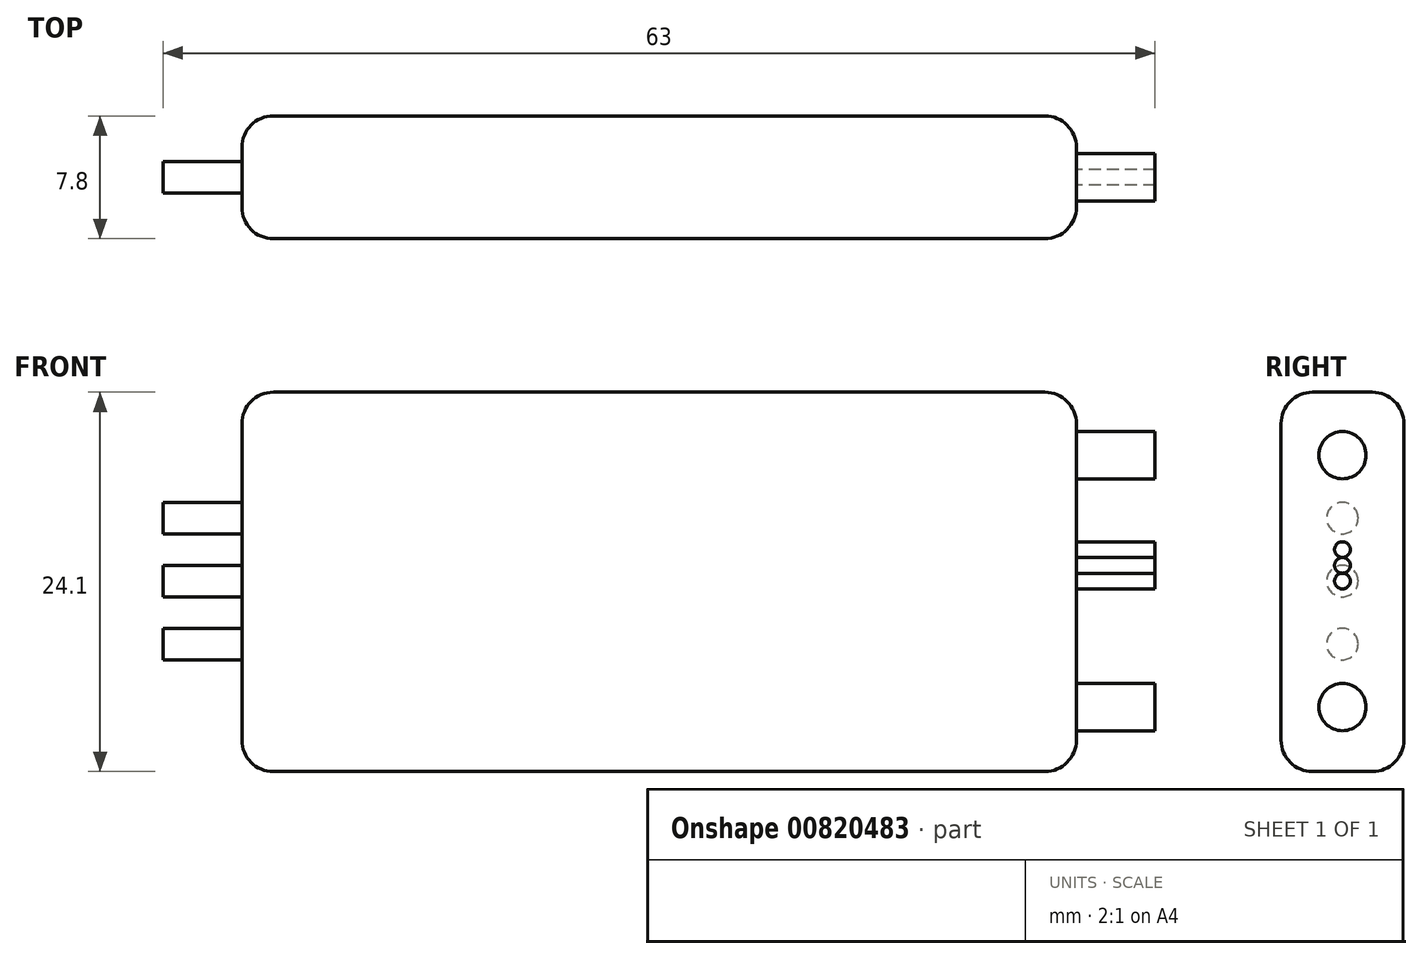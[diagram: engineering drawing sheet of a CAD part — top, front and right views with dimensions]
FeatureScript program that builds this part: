
annotation { "Feature Type Name" : "Feature", "Feature Type Description" : "" }
export const myFeature = defineFeature(function(context is Context, id is Id, definition is map)
    precondition{}
    {
        {
            var Q0;
            Q0=qCreatedBy(makeId("Front.planeOp"),FACE);
            var sketch = newSketch(context, id + "F0", { "sketchPlane" : qUnion([Q0])});
            skLineSegment(sketch, "E0.bottom", {"start": v(0, 0) * mm, "end": v(53, 0) * mm});
            skLineSegment(sketch, "E0.top", {"start": v(0, 24.1) * mm, "end": v(53, 24.1) * mm});
            skLineSegment(sketch, "E0.left", {"start": v(0, 0) * mm, "end": v(0, 24.1) * mm});
            skLineSegment(sketch, "E0.right", {"start": v(53, 0) * mm, "end": v(53, 24.1) * mm});
            skSolve(sketch);
        }
        {
            var Q0;
            Q0=makeQuery(id+"F0.imprint","IMPRINT",FACE,{"disambiguationData":[TD([[makeQuery(id+"F0.imprint","IMPRINT",EDGE,{"derivedFrom":sQuery(id+"F0.wireOp",EDGE,"E0.bottom")}),1.0]])]});
            extrude(context, id + "F1", {"entities" : qUnion([Q0]), "depth" : 7.8 * mm, "offsetDistance" : 25 * mm});
        }
        {
            var Q0;
            Q0=makeQuery(id+"F1.opExtrude","SWEPT_EDGE",EDGE,{"disambiguationData":[OSD([sQuery(id+"F0.wireOp",EDGE,"E0.bottom"),sQuery(id+"F0.wireOp",EDGE,"E0.right")])]});
            var Q1;
            Q1=makeQuery(id+"F1.opExtrude","SWEPT_EDGE",EDGE,{"disambiguationData":[OSD([sQuery(id+"F0.wireOp",EDGE,"E0.top"),sQuery(id+"F0.wireOp",EDGE,"E0.left")])]});
            var Q2;
            Q2=makeQuery(id+"F1.opExtrude","SWEPT_EDGE",EDGE,{"disambiguationData":[OSD([sQuery(id+"F0.wireOp",EDGE,"E0.top"),sQuery(id+"F0.wireOp",EDGE,"E0.right")])]});
            var Q3;
            Q3=makeQuery(id+"F1.opExtrude","SWEPT_EDGE",EDGE,{"disambiguationData":[OSD([sQuery(id+"F0.wireOp",EDGE,"E0.bottom"),sQuery(id+"F0.wireOp",EDGE,"E0.left")])]});
            var Q4;
            Q4=makeQuery(id+"F1.opExtrude","CAP_EDGE",EDGE,{"disambiguationData":[OSD([sQuery(id+"F0.wireOp",EDGE,"E0.bottom")])],"isStart":true});
            var Q5;
            Q5=makeQuery(id+"F1.opExtrude","CAP_EDGE",EDGE,{"disambiguationData":[OSD([sQuery(id+"F0.wireOp",EDGE,"E0.bottom")])],"isStart":false});
            var Q6;
            Q6=makeQuery(id+"F1.opExtrude","CAP_EDGE",EDGE,{"disambiguationData":[OSD([sQuery(id+"F0.wireOp",EDGE,"E0.top")])],"isStart":true});
            var Q7;
            Q7=makeQuery(id+"F1.opExtrude","CAP_EDGE",EDGE,{"disambiguationData":[OSD([sQuery(id+"F0.wireOp",EDGE,"E0.top")])],"isStart":false});
            var Q8;
            Q8=makeQuery(id+"F1.opExtrude","CAP_EDGE",EDGE,{"disambiguationData":[OSD([sQuery(id+"F0.wireOp",EDGE,"E0.left")])],"isStart":true});
            var Q9;
            Q9=makeQuery(id+"F1.opExtrude","CAP_EDGE",EDGE,{"disambiguationData":[OSD([sQuery(id+"F0.wireOp",EDGE,"E0.left")])],"isStart":false});
            var Q10;
            Q10=makeQuery(id+"F1.opExtrude","CAP_EDGE",EDGE,{"disambiguationData":[OSD([sQuery(id+"F0.wireOp",EDGE,"E0.right")])],"isStart":true});
            var Q11;
            Q11=makeQuery(id+"F1.opExtrude","CAP_EDGE",EDGE,{"disambiguationData":[OSD([sQuery(id+"F0.wireOp",EDGE,"E0.right")])],"isStart":false});
            fillet(context, id + "F2", {"entities" : qUnion([Q0, Q1, Q2, Q3, Q4, Q5, Q6, Q7, Q8, Q9, Q10, Q11]), "radius" : 2 * mm, "tangentPropagation" : true, "allowEdgeOverflow" : false});
        }
        {
            var Q0;
            Q0=makeQuery(id+"F1.opExtrude","SWEPT_FACE",FACE,{"disambiguationData":[OSD([sQuery(id+"F0.wireOp",EDGE,"E0.left")])]});
            var sketch = newSketch(context, id + "F3", { "sketchPlane" : qUnion([Q0])});
            skCircle(sketch, "E1", {"center": v(3.9, 16.1) * mm, "radius": 1 * mm});
            skCircle(sketch, "E2.0.1.0", {"center": v(3.9, 12.1) * mm, "radius": 1 * mm});
            skCircle(sketch, "E2.0.2.0", {"center": v(3.9, 8.1) * mm, "radius": 1 * mm});
            skLineSegment(sketch, "E2.direction1", {"start": v(3.9, 16.1) * mm, "end": v(6.9, 16.1) * mm, "construction": true});
            skLineSegment(sketch, "E2.direction2", {"start": v(3.9, 16.1) * mm, "end": v(3.9, 12.1) * mm, "construction": true});
            skSolve(sketch);
        }
        {
            var Q0;
            Q0=makeQuery(id+"F3.imprint","IMPRINT",FACE,{"disambiguationData":[TD([[makeQuery(id+"F3.imprint","IMPRINT",EDGE,{"derivedFrom":sQuery(id+"F3.wireOp",EDGE,"E1")}),1.0]])]});
            var Q1;
            Q1=makeQuery(id+"F3.imprint","IMPRINT",FACE,{"disambiguationData":[TD([[makeQuery(id+"F3.imprint","IMPRINT",EDGE,{"derivedFrom":sQuery(id+"F3.wireOp",EDGE,"E2.0.1.0")}),1.0]])]});
            var Q2;
            Q2=makeQuery(id+"F3.imprint","IMPRINT",FACE,{"disambiguationData":[TD([[makeQuery(id+"F3.imprint","IMPRINT",EDGE,{"derivedFrom":sQuery(id+"F3.wireOp",EDGE,"E2.0.2.0")}),1.0]])]});
            extrude(context, id + "F4", {"entities" : qUnion([Q0, Q1, Q2]), "depth" : 5 * mm, "offsetDistance" : 25 * mm});
        }
        {
            var Q0;
            Q0=makeQuery(id+"F1.opExtrude","SWEPT_FACE",FACE,{"disambiguationData":[OSD([sQuery(id+"F0.wireOp",EDGE,"E0.right")])]});
            var sketch = newSketch(context, id + "F5", { "sketchPlane" : qUnion([Q0])});
            skCircle(sketch, "E3", {"center": v(-3.9, 20.1) * mm, "radius": 1.5 * mm});
            skPoint(sketch, "E3.centerSnap0", {"position": v(-3.9, 22.1) * mm});
            skCircle(sketch, "E4.0.1.0", {"center": v(-3.9, 4.1) * mm, "radius": 1.5 * mm});
            skLineSegment(sketch, "E4.direction1", {"start": v(-3.9, 20.1) * mm, "end": v(21.1, 20.1) * mm, "construction": true});
            skLineSegment(sketch, "E4.direction2", {"start": v(-3.9, 20.1) * mm, "end": v(-3.9, 4.1) * mm, "construction": true});
            skCircle(sketch, "E5", {"center": v(-3.9, 14.1) * mm, "radius": 0.5 * mm});
            skCircle(sketch, "E6.0.1.0", {"center": v(-3.9, 13.1) * mm, "radius": 0.5 * mm});
            skCircle(sketch, "E6.0.2.0", {"center": v(-3.9, 12.1) * mm, "radius": 0.5 * mm});
            skLineSegment(sketch, "E6.direction1", {"start": v(-3.9, 14.1) * mm, "end": v(21.1, 14.1) * mm, "construction": true});
            skLineSegment(sketch, "E6.direction2", {"start": v(-3.9, 14.1) * mm, "end": v(-3.9, 13.1) * mm, "construction": true});
            skSolve(sketch);
        }
        {
            var Q0;
            Q0=makeQuery(id+"F5.imprint","IMPRINT",FACE,{"disambiguationData":[TD([[makeQuery(id+"F5.imprint","IMPRINT",EDGE,{"derivedFrom":sQuery(id+"F5.wireOp",EDGE,"E3")}),1.0]])]});
            var Q1;
            Q1=makeQuery(id+"F5.imprint","IMPRINT",FACE,{"disambiguationData":[TD([[makeQuery(id+"F5.imprint","IMPRINT",EDGE,{"derivedFrom":sQuery(id+"F5.wireOp",EDGE,"E5")}),1.0]])]});
            var Q2;
            {var subQ0=sQuery(id+"F5.wireOp",EDGE,"E6.0.1.0");var subQ1=makeQuery(id+"F5.imprint","INTERSECT",VERTEX,{"derivedFrom":[sQuery(id+"F5.wireOp",EDGE,"E5"),subQ0]});Q2=makeQuery(id+"F5.imprint","IMPRINT",FACE,{"disambiguationData":[TD([[makeQuery(id+"F5.imprint","IMPRINT",EDGE,{"disambiguationData":[TD([[subQ1,-1.0]])],"derivedFrom":subQ0}),1.0]])]});}
            var Q3;
            Q3=makeQuery(id+"F5.imprint","IMPRINT",FACE,{"disambiguationData":[TD([[makeQuery(id+"F5.imprint","IMPRINT",EDGE,{"derivedFrom":sQuery(id+"F5.wireOp",EDGE,"E6.0.2.0")}),1.0]])]});
            var Q4;
            Q4=makeQuery(id+"F5.imprint","IMPRINT",FACE,{"disambiguationData":[TD([[makeQuery(id+"F5.imprint","IMPRINT",EDGE,{"derivedFrom":sQuery(id+"F5.wireOp",EDGE,"E4.0.1.0")}),1.0]])]});
            extrude(context, id + "F6", {"entities" : qUnion([Q0, Q1, Q2, Q3, Q4]), "depth" : 5 * mm, "offsetDistance" : 25 * mm});
        }
    });
